# Revit family: 94518205
name_source: partatom
category: Componentes de gabinete
revit_build: Autodesk Revit 2016 (Build: 20150220_1215(x64)
units: mm (PartAtom-declared; Revit-internal decimal feet)

## family parameters
Com base no plano de trabalho = Não
Compartilhado = Não
Corte com vazios quando carregados = Não
Ponto de cálculo do ambiente = Não
Sempre na vertical = Sim

## types (1)
- Clean Square - 94518/205
    Altura = 248  [stored 0.813648 ft]
    Comentários de tipos = Ler Manual de Instalação
    Concluir = Aço Inox AISI 304
    Código de montagem = 94518/205
    Descrição = Clean Square - 94518/205
    Desenvolvedor = Factory Cursos & Desenvolvimento
    Fabricante = Tramontina
    Largura = 248  [stored 0.813648 ft]
    Linear = 229
    Modelo = Clean Square - 94518/205
    Site do desenvolvedor = www.factorycursos.com.br
    Tipo de imagem = <Nenhum>
    URL = www.tramontina.com.br

note: [stored X ft] marks values corroborated as IEEE doubles in the binary element streams (Revit-internal decimal feet)
